# Revit family: P710103-031-30
name_source: partatom
category: Lighting Fixtures
units: mm (PartAtom-declared; Revit-internal decimal feet)

## family parameters
Cut with Voids When Loaded = No
Host = Face
Light Source = No
OmniClass Number = 23.80.70.11.14.17
OmniClass Title = Direct/Indirect
Part Type = Normal
Room Calculation Point = No
Round Connector Dimension = Use Diameter
Shared = Yes

## types (1)
- P710103-031-30
    Apparent Load = 13 VA
    Assembly Code = D5020200
    Connector Description = Lighting Connector
    Default Elevation = 48 "
    Depth = 3.3 "
    Description = Quadrant LED Collection Two-Light Matte Black Modern Style Wall Light
    Features = Quadrant LED Collection 2-Light Matte Black Frosted Glass Modern Wall Light
Application: Define space with a minimalist approach with the Quadrant LED Collection 2-Light Matte Black Frosted Glass Modern Wall Light ideal for any entryway, hallway, foyer, bedroom, sitting room, living room, or bathroom.
Styles: Perfect for modern and contemporary style settings.
Finish: Metal struts coated in a classic matte black finish are arranged in a modern geometric design giving the layered frame an impression of substance in space.
Materials: Constructed from steel to ensure a long product lifespan
can be installed as a wall or ceiling mount.
Glass/Shades: Integrated LED lights tip the end of the metal struts and glow from within the crisp frosted glass shades that create airy illumination.
Bulbs: For ideal illumination, 2 integrated LEDs are included (13w)
3000K
90CRI
686 delivered lumens
dimmable.
Dimensions: Measures 8-inch width by 24-inch height by 3-5/16-inch depth
Certifications: cETLus damp location listed, meets California Title 24 JA8-2019.
Pairs With: Pairs with a variety of Progress Lighting fixtures.
    Fixture distribution = Direct
    Glass = Paint - Hubbell - White Texture
    Gold = Hubbell - Gold
    Height = 24 "
    Housing Material = Paint - Hubbell - Textured Camera Black
    Lamp = LED
    Length = 8.06 "
    Load Classification = Lighting
    Manufacturer = Progress Lighting
    Model = P710103-031-30
    Power Factor = 1
    Product Documentation Link = https://hubbellcdn.com
    Product Link = https://www.hubbell.com
    Support = Paint - Hubbell - Dark Nickel
    URL = https://www.hubbell.com
    Voltage = 120 V
    Warranty = 5 years Warranty
    Wattage Comments = 13W
    Watts = 13 W

## geometry (parser evidence)
native form markers: Sweep x4
no freeform markers — native parametric forms only
